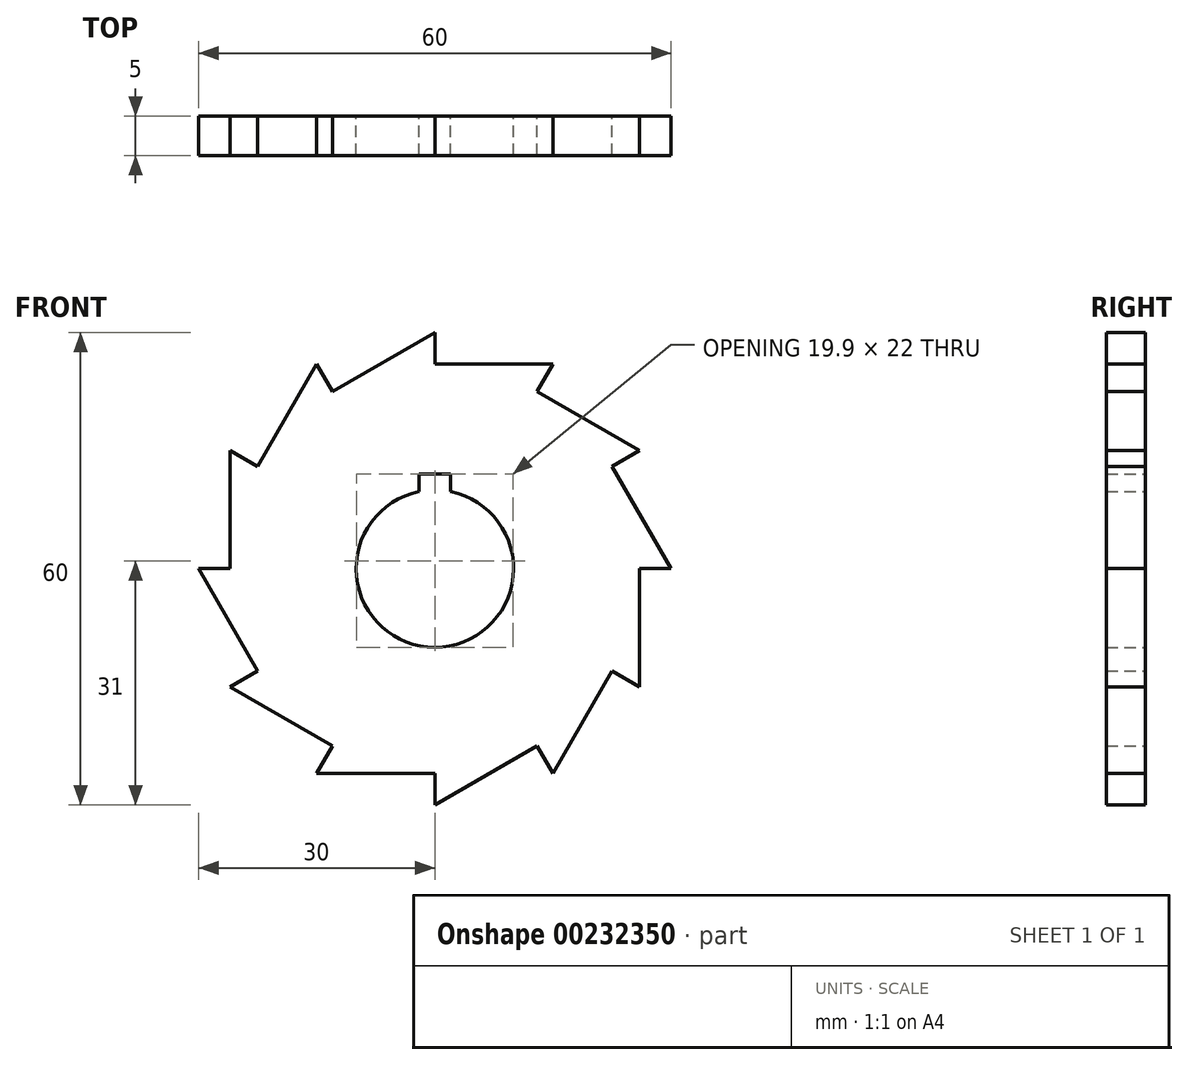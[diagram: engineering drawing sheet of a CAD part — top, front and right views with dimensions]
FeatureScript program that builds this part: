
annotation { "Feature Type Name" : "Feature", "Feature Type Description" : "" }
export const myFeature = defineFeature(function(context is Context, id is Id, definition is map)
    precondition{}
    {
        {
            var Q0;
            Q0=qCreatedBy(makeId("Front.planeOp"),FACE);
            var sketch = newSketch(context, id + "F0", { "sketchPlane" : qUnion([Q0])});
            skArc(sketch, "E0", {"start": v(-2, 9.8) * mm, "mid": v(0, -10) * mm, "end": v(2, 9.8) * mm});
            skLineSegment(sketch, "E1", {"start": v(-2, 9.8) * mm, "end": v(-2, 12) * mm});
            skLineSegment(sketch, "E2", {"start": v(-2, 12) * mm, "end": v(0, 12) * mm});
            skCircle(sketch, "E3", {"center": v(0, 0) * mm, "radius": 30 * mm, "construction": true});
            skLineSegment(sketch, "E4", {"start": v(0, 0) * mm, "end": v(11.5, 19.9) * mm, "construction": true});
            skLineSegment(sketch, "E5", {"start": v(0, 0) * mm, "end": v(21.43, 12.37) * mm, "construction": true});
            skLineSegment(sketch, "E6", {"start": v(25.98, 15) * mm, "end": v(13, 22.5) * mm});
            skLineSegment(sketch, "E7", {"start": v(13, 22.5) * mm, "end": v(15, 25.98) * mm});
            skLineSegment(sketch, "E8.1.0", {"start": v(0, 25.98) * mm, "end": v(0, 30) * mm});
            skLineSegment(sketch, "E8.1.1", {"start": v(15, 25.98) * mm, "end": v(0, 25.98) * mm});
            skLineSegment(sketch, "E8.2.0", {"start": v(-13, 22.5) * mm, "end": v(-15, 25.98) * mm});
            skLineSegment(sketch, "E8.2.1", {"start": v(0, 30) * mm, "end": v(-13, 22.5) * mm});
            skLineSegment(sketch, "E8.3.0", {"start": v(-22.5, 13) * mm, "end": v(-25.98, 15) * mm});
            skLineSegment(sketch, "E8.3.1", {"start": v(-15, 25.98) * mm, "end": v(-22.5, 13) * mm});
            skLineSegment(sketch, "E8.4.0", {"start": v(-25.98, 0) * mm, "end": v(-30, 0) * mm});
            skLineSegment(sketch, "E8.4.1", {"start": v(-25.98, 15) * mm, "end": v(-25.98, 0) * mm});
            skLineSegment(sketch, "E8.5.0", {"start": v(-22.5, -13) * mm, "end": v(-25.98, -15) * mm});
            skLineSegment(sketch, "E8.5.1", {"start": v(-30, 0) * mm, "end": v(-22.5, -13) * mm});
            skLineSegment(sketch, "E8.6.0", {"start": v(-13, -22.5) * mm, "end": v(-15, -25.98) * mm});
            skLineSegment(sketch, "E8.6.1", {"start": v(-25.98, -15) * mm, "end": v(-13, -22.5) * mm});
            skLineSegment(sketch, "E8.7.0", {"start": v(0, -25.98) * mm, "end": v(0, -30) * mm});
            skLineSegment(sketch, "E8.7.1", {"start": v(-15, -25.98) * mm, "end": v(0, -25.98) * mm});
            skLineSegment(sketch, "E8.8.0", {"start": v(13, -22.5) * mm, "end": v(15, -25.98) * mm});
            skLineSegment(sketch, "E8.8.1", {"start": v(0, -30) * mm, "end": v(13, -22.5) * mm});
            skLineSegment(sketch, "E8.9.0", {"start": v(22.5, -13) * mm, "end": v(25.98, -15) * mm});
            skLineSegment(sketch, "E8.9.1", {"start": v(15, -25.98) * mm, "end": v(22.5, -13) * mm});
            skLineSegment(sketch, "E8.10.0", {"start": v(25.98, 0) * mm, "end": v(30, 0) * mm});
            skLineSegment(sketch, "E8.10.1", {"start": v(25.98, -15) * mm, "end": v(25.98, 0) * mm});
            skLineSegment(sketch, "E8.11.0", {"start": v(22.5, 13) * mm, "end": v(25.98, 15) * mm});
            skLineSegment(sketch, "E8.11.1", {"start": v(30, 0) * mm, "end": v(22.5, 13) * mm});
            skLineSegment(sketch, "E9.MirrorCS", {"start": v(2, 12) * mm, "end": v(0, 12) * mm});
            skLineSegment(sketch, "E10.MirrorCS", {"start": v(2, 9.8) * mm, "end": v(2, 12) * mm});
            skSolve(sketch);
        }
        {
            var Q0;
            Q0=makeQuery(id+"F0.imprint","IMPRINT",FACE,{"disambiguationData":[TD([[makeQuery(id+"F0.imprint","IMPRINT",EDGE,{"derivedFrom":sQuery(id+"F0.wireOp",EDGE,"E0")}),-1.0]])]});
            extrude(context, id + "F1", {"entities" : qUnion([Q0]), "depth" : 5 * mm});
        }
    });
